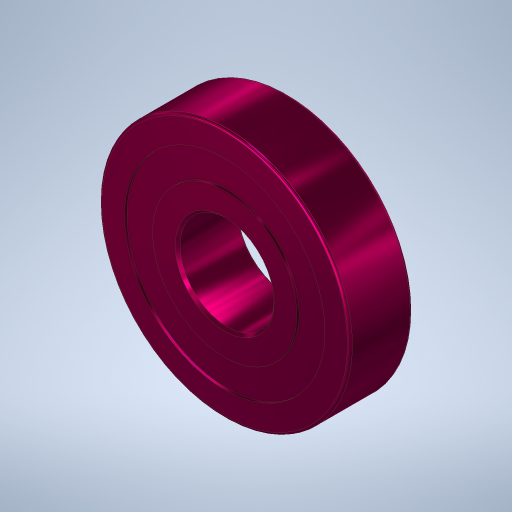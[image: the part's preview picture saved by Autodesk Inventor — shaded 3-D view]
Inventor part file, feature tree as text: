
AUTODESK INVENTOR PART (.ipt)
format: ipt  version: 2023.1 (Build 271208000, 208)  size: 315,392 bytes
history: native  units: in
note: dims shown in document units (in); Inventor stores cm internally (conversion verified against a paired STEP export)
features: extrude x2, sketch x2, fillet x1, chamfer x1, plane x1, projected_geometry x1
ambient origin geometry x8: Origin, YZ Plane, XZ Plane, XY Plane, X Axis, Y Axis, Z Axis, Center Point
bodies: Solid1 (feature_tree)
feature tree (8):
  extrude  "Extrusion1"  Depth=0.5in
  fillet  "Fillet1"  Radius=0.05in
  chamfer  "Chamfer1"  Distance=0.125in
  plane  "Work Plane1"
  extrude  "Extrusion2"  Depth=0.005in
  sketch  "Sketch1"  dims[d0=0.1875in d1=0.5in d2=0.05in]
  sketch  "Sketch2"  dims[d3=0.05in d4=0.125in d5=0.0in d6=0.005in d7=0.005in d8=0.125in d9=45.0deg d10=0.115in d11=0.0in]
  projected_geometry  "Project Cut Edges1"
